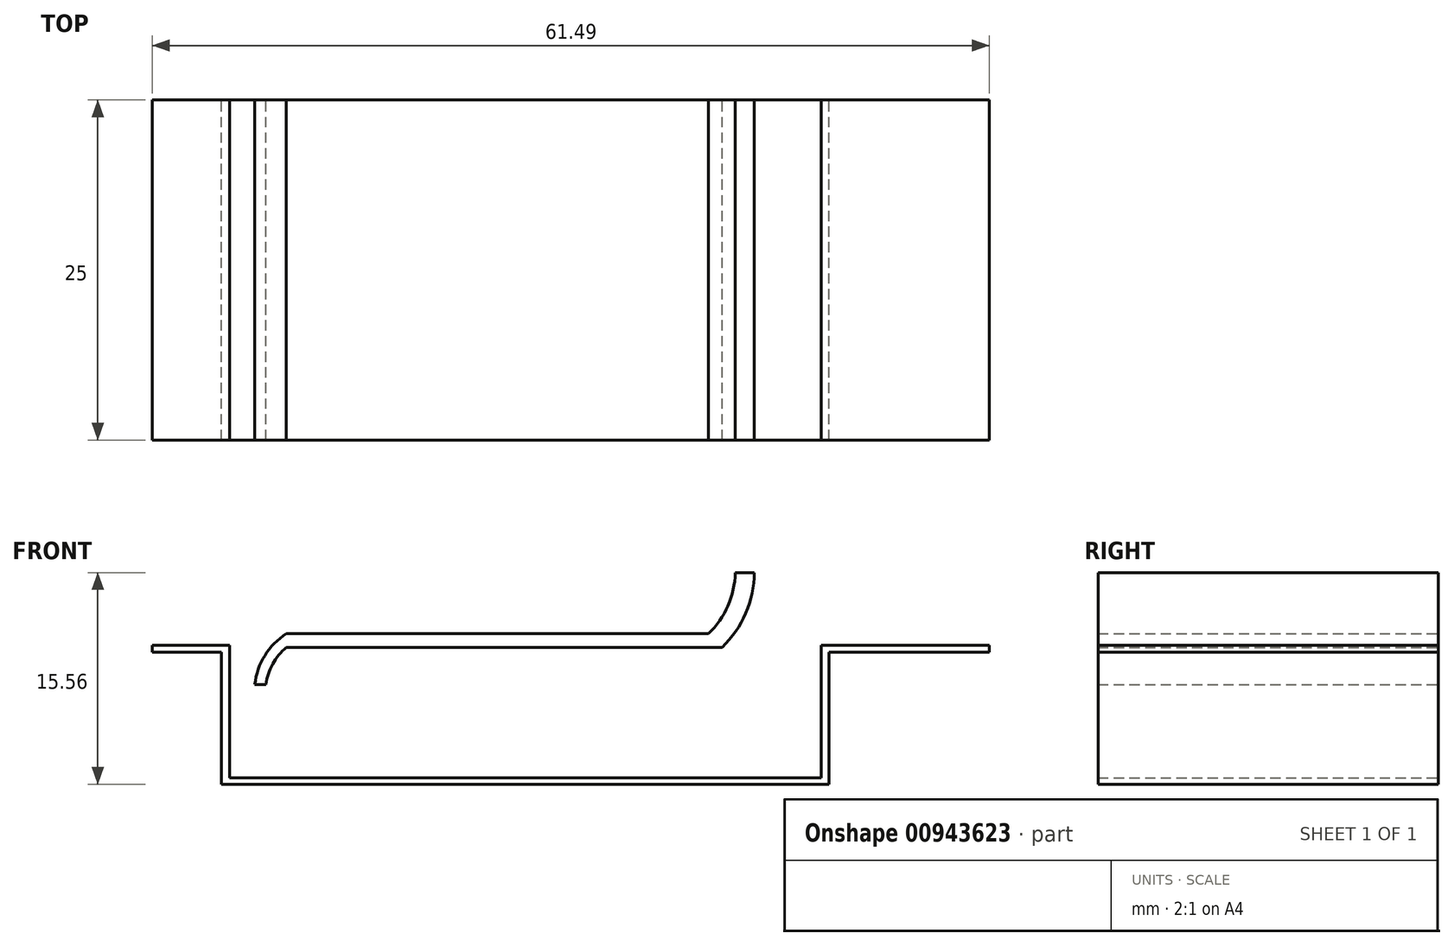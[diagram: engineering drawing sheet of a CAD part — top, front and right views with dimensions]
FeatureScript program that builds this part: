
annotation { "Feature Type Name" : "Feature", "Feature Type Description" : "" }
export const myFeature = defineFeature(function(context is Context, id is Id, definition is map)
    precondition{}
    {
        {
            var Q0;
            Q0=qCreatedBy(makeId("Front.planeOp"),FACE);
            var sketch = newSketch(context, id + "F0", { "sketchPlane" : qUnion([Q0])});
            skLineSegment(sketch, "E0.bottom", {"start": v(-16.82, 2.74) * mm, "end": v(-48.83, 2.74) * mm});
            skLineSegment(sketch, "E1.left", {"start": v(-15.82, 3.74) * mm, "end": v(-15.82, 3.74) * mm});
            skLineSegment(sketch, "E1.right", {"start": v(-17.82, 3.74) * mm, "end": v(-17.82, 3.74) * mm});
            skPoint(sketch, "E1.middle", {"position": v(-16.82, 3.74) * mm});
            skLineSegment(sketch, "E2.left", {"start": v(-16.82, 3.74) * mm, "end": v(-16.82, 3.74) * mm});
            skLineSegment(sketch, "E3.top", {"start": v(-16.28, 6.04) * mm, "end": v(-15.82, 6.04) * mm});
            skArc(sketch, "E4", {"start": v(-16.82, 2.74) * mm, "mid": v(-15.08, 5.25) * mm, "end": v(-14.44, 8.23) * mm});
            skArc(sketch, "E5", {"start": v(-17.82, 3.74) * mm, "mid": v(-16.39, 5.79) * mm, "end": v(-15.86, 8.23) * mm});
            skLineSegment(sketch, "E6", {"start": v(-15.86, 8.23) * mm, "end": v(-14.44, 8.23) * mm});
            skLineSegment(sketch, "E7.trimOffspring", {"start": v(-17.82, 3.74) * mm, "end": v(-48.83, 3.74) * mm});
            skArc(sketch, "E8", {"start": v(-48.83, 2.74) * mm, "mid": v(-49.84, 1.51) * mm, "end": v(-50.34, 0) * mm});
            skPoint(sketch, "E8.first.point", {"position": v(-43.3, 2.74) * mm});
            skPoint(sketch, "E8.third.point", {"position": v(-46.25, 3.74) * mm});
            skArc(sketch, "E9", {"start": v(-48.83, 3.74) * mm, "mid": v(-50.41, 2.13) * mm, "end": v(-51.15, 0) * mm});
            skArc(sketch, "E10.trimOffspring", {"start": v(-45.88, 3.74) * mm, "mid": v(-46.07, 3.75) * mm, "end": v(-46.25, 3.74) * mm});
            skLineSegment(sketch, "E11", {"start": v(-50.34, 0) * mm, "end": v(-51.15, 0) * mm});
            skSolve(sketch);
        }
        {
            var Q0;
            Q0=makeQuery(id+"F0.imprint","IMPRINT",FACE,{"disambiguationData":[TD([[makeQuery(id+"F0.imprint","IMPRINT",EDGE,{"derivedFrom":sQuery(id+"F0.wireOp",EDGE,"E0.bottom")}),-1.0]])]});
            extrude(context, id + "F1", {"entities" : qUnion([Q0]), "depth" : 25 * mm, "offsetDistance" : 25 * mm});
        }
        {
            var Q0;
            Q0=qCreatedBy(makeId("Front.planeOp"),FACE);
            var sketch = newSketch(context, id + "F2", { "sketchPlane" : qUnion([Q0])});
            skLineSegment(sketch, "E12", {"start": v(-53, 2.9) * mm, "end": v(-53, -6.85) * mm});
            skLineSegment(sketch, "E13", {"start": v(-53, -6.85) * mm, "end": v(-9.54, -6.85) * mm});
            skLineSegment(sketch, "E14", {"start": v(-9.54, -6.85) * mm, "end": v(-9.54, 2.9) * mm});
            skLineSegment(sketch, "E15", {"start": v(-9.54, 2.9) * mm, "end": v(2.81, 2.9) * mm});
            skLineSegment(sketch, "E16", {"start": v(2.81, 2.9) * mm, "end": v(2.81, 2.38) * mm});
            skLineSegment(sketch, "E17", {"start": v(2.81, 2.38) * mm, "end": v(-8.96, 2.38) * mm});
            skLineSegment(sketch, "E18", {"start": v(-8.96, 2.38) * mm, "end": v(-8.96, -7.33) * mm});
            skLineSegment(sketch, "E19", {"start": v(-8.96, -7.33) * mm, "end": v(-53.61, -7.33) * mm});
            skLineSegment(sketch, "E20", {"start": v(-53.61, -7.33) * mm, "end": v(-53.61, 2.38) * mm});
            skLineSegment(sketch, "E21", {"start": v(-53, 2.9) * mm, "end": v(-58.68, 2.9) * mm});
            skLineSegment(sketch, "E22", {"start": v(-58.68, 2.9) * mm, "end": v(-58.68, 2.38) * mm});
            skLineSegment(sketch, "E23", {"start": v(-58.68, 2.38) * mm, "end": v(-53.61, 2.38) * mm});
            skSolve(sketch);
        }
        {
            var Q0;
            Q0 = qSketchRegion(id + "F2", true);
            extrude(context, id + "F3", {"entities" : qUnion([Q0]), "depth" : 25 * mm, "offsetDistance" : 25 * mm});
        }
    });
